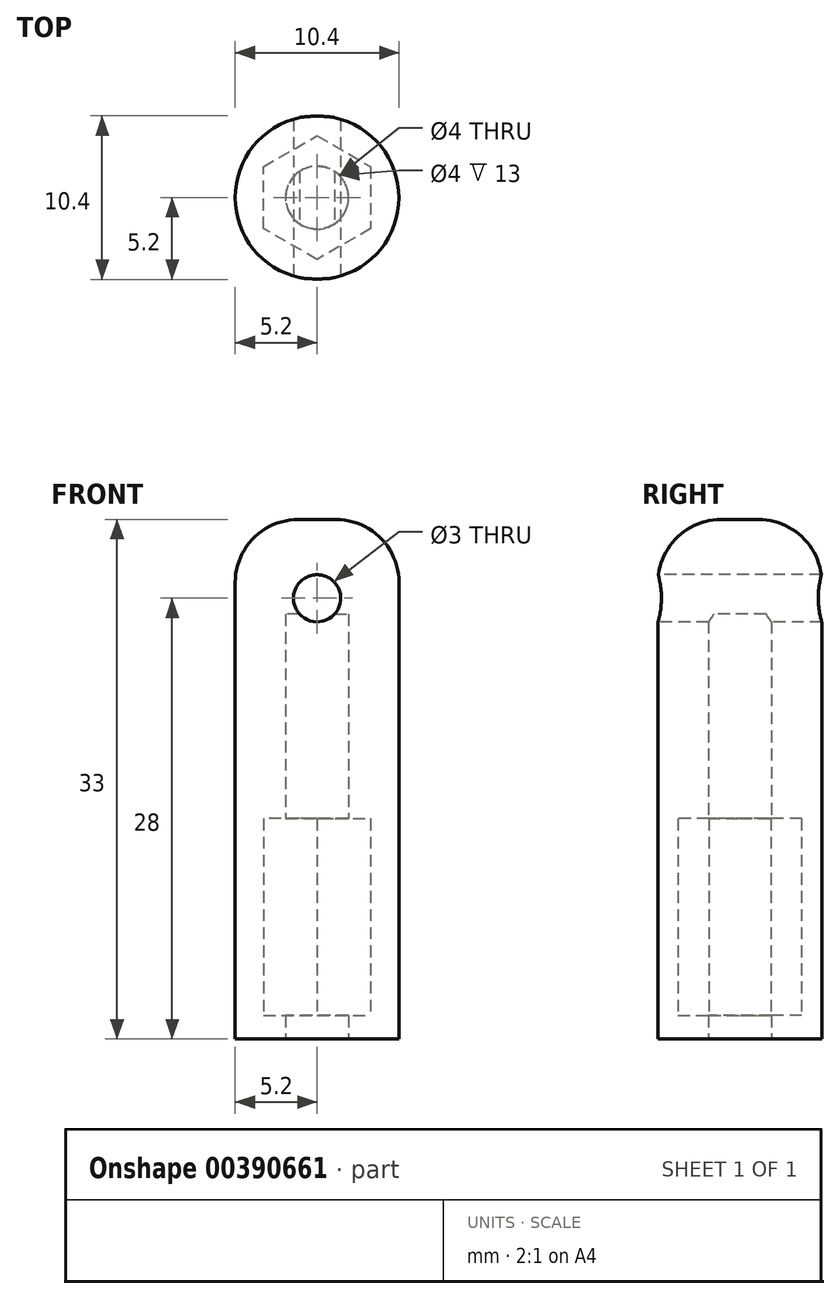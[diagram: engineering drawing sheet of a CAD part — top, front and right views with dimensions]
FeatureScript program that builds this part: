
annotation { "Feature Type Name" : "Feature", "Feature Type Description" : "" }
export const myFeature = defineFeature(function(context is Context, id is Id, definition is map)
    precondition{}
    {
        {
            var Q0;
            Q0=qCreatedBy(makeId("Top.planeOp"),FACE);
            var sketch = newSketch(context, id + "F0", { "sketchPlane" : qUnion([Q0])});
            skCircle(sketch, "E0", {"center": v(0, 0) * mm, "radius": 5.2 * mm});
            skCircle(sketch, "E1", {"center": v(0, 0) * mm, "radius": 2 * mm});
            skSolve(sketch);
        }
        {
            var Q0;
            Q0=qSketchRegion(id+"F0",true);
            extrude(context, id + "F1", {"entities" : qUnion([Q0]), "depth" : 1.5 * mm, "offsetDistance" : 25 * mm});
        }
        {
            var Q0;
            Q0=makeQuery(id+"F1.opExtrude","CAP_FACE",FACE,{"disambiguationData":[OSD([sQuery(id+"F0.wireOp",EDGE,"E0")])],"isStart":false});
            var sketch = newSketch(context, id + "F2", { "sketchPlane" : qUnion([Q0])});
            skCircle(sketch, "E2.cCircle", {"center": v(0, 0) * mm, "radius": 3.4 * mm, "construction": true});
            skLineSegment(sketch, "E2.0", {"start": v(3.4, 1.96) * mm, "end": v(3.4, -1.96) * mm});
            skLineSegment(sketch, "E2.1", {"start": v(3.4, -1.96) * mm, "end": v(0, -3.93) * mm});
            skLineSegment(sketch, "E2.2", {"start": v(0, -3.93) * mm, "end": v(-3.4, -1.96) * mm});
            skLineSegment(sketch, "E2.3", {"start": v(-3.4, -1.96) * mm, "end": v(-3.4, 1.96) * mm});
            skLineSegment(sketch, "E2.4", {"start": v(-3.4, 1.96) * mm, "end": v(0, 3.93) * mm});
            skLineSegment(sketch, "E2.5", {"start": v(0, 3.93) * mm, "end": v(3.4, 1.96) * mm});
            skPoint(sketch, "E2.0.midPoint", {"position": v(3.4, 0) * mm});
            skSolve(sketch);
        }
        {
            var Q0;
            Q0=makeQuery(id+"F2.imprint","IMPRINT",FACE,{"disambiguationData":[TD([[makeQuery(id+"F2.imprint","IMPRINT",EDGE,{"derivedFrom":sQuery(id+"F2.wireOp",EDGE,"E2.0")}),1.0]])]});
            extrude(context, id + "F3", {"entities" : qUnion([Q0]), "operationType" : NewBodyOperationType.ADD, "depth" : 12.5 * mm, "offsetDistance" : 25 * mm});
        }
        {
            var Q0;
            Q0=makeQuery(id+"F3.opExtrude","CAP_FACE",FACE,{"disambiguationData":[OSD([sQuery(id+"F0.wireOp",EDGE,"E0"),sQuery(id+"F2.wireOp",EDGE,"E2.0"),sQuery(id+"F2.wireOp",EDGE,"E2.1"),sQuery(id+"F2.wireOp",EDGE,"E2.2"),sQuery(id+"F2.wireOp",EDGE,"E2.3"),sQuery(id+"F2.wireOp",EDGE,"E2.4"),sQuery(id+"F2.wireOp",EDGE,"E2.5")])],"isStart":false});
            var sketch = newSketch(context, id + "F4", { "sketchPlane" : qUnion([Q0])});
            skCircle(sketch, "E3", {"center": v(0, 0) * mm, "radius": 2 * mm});
            skCircle(sketch, "E4", {"center": v(0, 0) * mm, "radius": 5.2 * mm});
            skSolve(sketch);
        }
        {
            var Q0;
            Q0=makeQuery(id+"F4.imprint","IMPRINT",FACE,{"disambiguationData":[TD([[makeQuery(id+"F4.imprint","IMPRINT",EDGE,{"derivedFrom":sQuery(id+"F4.wireOp",EDGE,"E3")}),-1.0]])]});
            var Q1;
            Q1=makeQuery(id+"F4.imprint","IMPRINT",FACE,{"disambiguationData":[TD([[makeQuery(id+"F4.imprint","IMPRINT",EDGE,{"derivedFrom":sQuery(id+"F4.wireOp",EDGE,"E4")}),1.0]])]});
            extrude(context, id + "F5", {"entities" : qUnion([Q0, Q1]), "operationType" : NewBodyOperationType.ADD, "depth" : 13 * mm, "offsetDistance" : 25 * mm});
        }
        {
            var Q0;
            Q0=makeQuery(id+"F5.opExtrude","CAP_FACE",FACE,{"disambiguationData":[OSD([sQuery(id+"F4.wireOp",EDGE,"E3"),sQuery(id+"F4.wireOp",EDGE,"E4")])],"isStart":false});
            var sketch = newSketch(context, id + "F6", { "sketchPlane" : qUnion([Q0])});
            skCircle(sketch, "E5", {"center": v(0, 0) * mm, "radius": 5.2 * mm});
            skSolve(sketch);
        }
        {
            var Q0;
            Q0=qSketchRegion(id+"F6",true);
            extrude(context, id + "F7", {"entities" : qUnion([Q0]), "operationType" : NewBodyOperationType.ADD, "depth" : 6 * mm, "offsetDistance" : 25 * mm});
        }
        {
            var Q0;
            Q0=makeQuery(id+"F0wGZmDVDnfMHNC_1.opExtrude","CAP_EDGE",EDGE,{"disambiguationData":[OSD([sQuery(id+"F4.wireOp",EDGE,"E4")])],"isStart":false});
            var Q1;
            Q1=makeQuery(id+"F7.opExtrude","CAP_EDGE",EDGE,{"disambiguationData":[OSD([sQuery(id+"F6.wireOp",EDGE,"E5")])],"isStart":false});
            fillet(context, id + "F8", {"entities" : qUnion([Q0, Q1]), "radius" : 4 * mm, "tangentPropagation" : true, "allowEdgeOverflow" : false});
        }
        {
            var Q0;
            Q0=qCreatedBy(makeId("Front.planeOp"),FACE);
            var sketch = newSketch(context, id + "F9", { "sketchPlane" : qUnion([Q0])});
            skCircle(sketch, "E6", {"center": v(0, 28) * mm, "radius": 1.5 * mm});
            skSolve(sketch);
        }
        {
            var Q0;
            Q0=qSketchRegion(id+"F9",true);
            extrude(context, id + "F10", {"entities" : qUnion([Q0]), "operationType" : NewBodyOperationType.REMOVE, "oppositeDirection" : true, "depth" : 25 * mm, "offsetDistance" : 25 * mm, "symmetric" : true});
        }
    });
